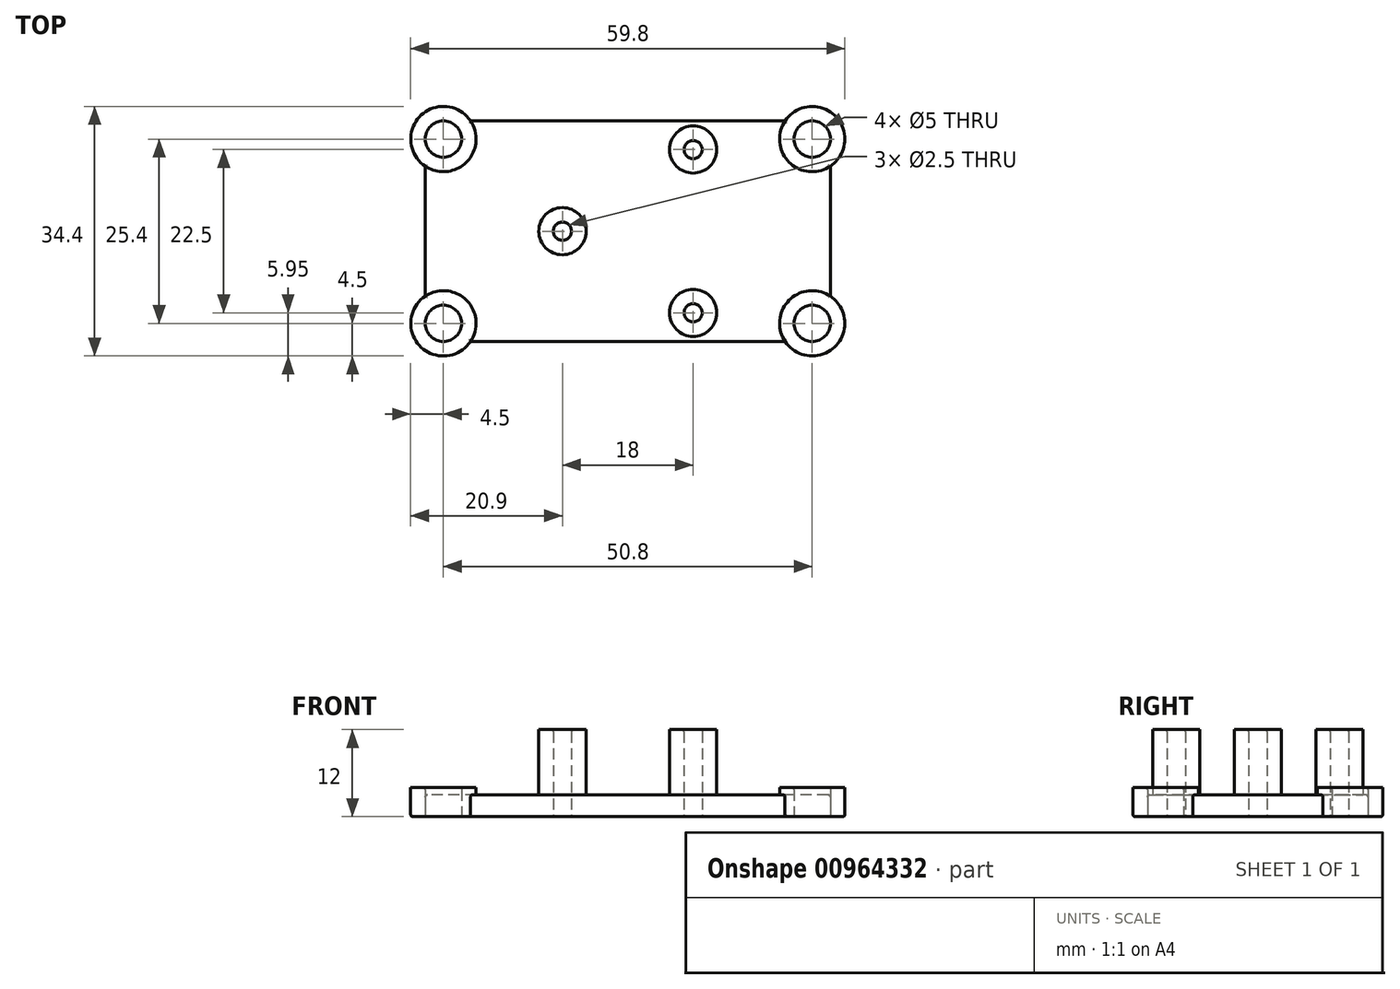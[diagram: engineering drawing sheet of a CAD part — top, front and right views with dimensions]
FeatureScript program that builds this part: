
annotation { "Feature Type Name" : "Feature", "Feature Type Description" : "" }
export const myFeature = defineFeature(function(context is Context, id is Id, definition is map)
    precondition{}
    {
        {
            var Q0;
            Q0=qCreatedBy(makeId("Top.planeOp"),FACE);
            var sketch = newSketch(context, id + "F0", { "sketchPlane" : qUnion([Q0])});
            skLineSegment(sketch, "E0.bottom", {"start": v(0, 0) * mm, "end": v(-18, 0) * mm, "construction": true});
            skLineSegment(sketch, "E0.top", {"start": v(0, 22.5) * mm, "end": v(-18, 22.5) * mm, "construction": true});
            skLineSegment(sketch, "E0.left", {"start": v(0, 0) * mm, "end": v(0, 22.5) * mm, "construction": true});
            skLineSegment(sketch, "E0.right", {"start": v(-18, 0) * mm, "end": v(-18, 22.5) * mm, "construction": true});
            skLineSegment(sketch, "E1", {"start": v(0, 11.25) * mm, "end": v(-18, 11.25) * mm, "construction": true});
            skLineSegment(sketch, "E2", {"start": v(-18, 11.25) * mm, "end": v(0, 22.5) * mm, "construction": true});
            skCircle(sketch, "E3", {"center": v(-18, 11.25) * mm, "radius": 1.25 * mm});
            skCircle(sketch, "E4", {"center": v(0, 22.5) * mm, "radius": 1.25 * mm});
            skCircle(sketch, "E5", {"center": v(0, 0) * mm, "radius": 1.25 * mm});
            skCircle(sketch, "E6", {"center": v(0, 22.5) * mm, "radius": 3.25 * mm});
            skCircle(sketch, "E7", {"center": v(-18, 11.25) * mm, "radius": 3.25 * mm});
            skCircle(sketch, "E8", {"center": v(0, 0) * mm, "radius": 3.25 * mm});
            skLineSegment(sketch, "E9.bottom", {"start": v(16.4, -1.45) * mm, "end": v(-34.4, -1.45) * mm, "construction": true});
            skLineSegment(sketch, "E9.top", {"start": v(16.4, 23.95) * mm, "end": v(-34.4, 23.95) * mm, "construction": true});
            skLineSegment(sketch, "E9.left", {"start": v(16.4, -1.45) * mm, "end": v(16.4, 23.95) * mm, "construction": true});
            skLineSegment(sketch, "E9.right", {"start": v(-34.4, -1.45) * mm, "end": v(-34.4, 23.95) * mm, "construction": true});
            skPoint(sketch, "E9.middle", {"position": v(-9, 11.25) * mm});
            skCircle(sketch, "E10", {"center": v(-34.4, 23.95) * mm, "radius": 2.5 * mm});
            skCircle(sketch, "E11", {"center": v(-34.4, -1.45) * mm, "radius": 2.5 * mm});
            skCircle(sketch, "E12", {"center": v(16.4, -1.45) * mm, "radius": 2.5 * mm});
            skCircle(sketch, "E13", {"center": v(16.4, 23.95) * mm, "radius": 2.5 * mm});
            skCircle(sketch, "E14", {"center": v(-34.4, 23.95) * mm, "radius": 4.5 * mm});
            skCircle(sketch, "E15", {"center": v(16.4, 23.95) * mm, "radius": 4.5 * mm});
            skCircle(sketch, "E16", {"center": v(-34.4, -1.45) * mm, "radius": 4.5 * mm});
            skCircle(sketch, "E17", {"center": v(16.4, -1.45) * mm, "radius": 4.5 * mm});
            skLineSegment(sketch, "E18.bottom", {"start": v(-34, 29.25) * mm, "end": v(16, 29.25) * mm, "construction": true});
            skLineSegment(sketch, "E18.top", {"start": v(-34, -6.75) * mm, "end": v(16, -6.75) * mm, "construction": true});
            skLineSegment(sketch, "E18.left", {"start": v(-34, 29.25) * mm, "end": v(-34, -6.75) * mm, "construction": true});
            skLineSegment(sketch, "E18.right", {"start": v(16, 29.25) * mm, "end": v(16, -6.75) * mm, "construction": true});
            skLineSegment(sketch, "E19", {"start": v(-34, 11.25) * mm, "end": v(16, 11.25) * mm, "construction": true});
            skLineSegment(sketch, "E20", {"start": v(-30.66, -3.95) * mm, "end": v(12.66, -3.95) * mm});
            skLineSegment(sketch, "E21", {"start": v(-36.9, 20.2) * mm, "end": v(-36.9, 2.3) * mm});
            skLineSegment(sketch, "E22", {"start": v(-30.66, 26.45) * mm, "end": v(12.66, 26.45) * mm});
            skLineSegment(sketch, "E23", {"start": v(18.9, 20.2) * mm, "end": v(18.9, 2.3) * mm});
            skSolve(sketch);
        }
        {
            var Q0;
            Q0=makeQuery(id+"F0.imprint","IMPRINT",FACE,{"disambiguationData":[TD([[makeQuery(id+"F0.imprint","IMPRINT",EDGE,{"derivedFrom":sQuery(id+"F0.wireOp",EDGE,"E6")}),-1.0]])]});
            extrude(context, id + "F1", {"entities" : qUnion([Q0]), "depth" : 3 * mm, "offsetDistance" : 25 * mm});
        }
        {
            var Q0;
            Q0=makeQuery(id+"F0.imprint","IMPRINT",FACE,{"disambiguationData":[TD([[makeQuery(id+"F0.imprint","IMPRINT",EDGE,{"derivedFrom":sQuery(id+"F0.wireOp",EDGE,"E4")}),-1.0]])]});
            var Q1;
            Q1=makeQuery(id+"F0.imprint","IMPRINT",FACE,{"disambiguationData":[TD([[makeQuery(id+"F0.imprint","IMPRINT",EDGE,{"derivedFrom":sQuery(id+"F0.wireOp",EDGE,"E3")}),-1.0]])]});
            var Q2;
            Q2=makeQuery(id+"F0.imprint","IMPRINT",FACE,{"disambiguationData":[TD([[makeQuery(id+"F0.imprint","IMPRINT",EDGE,{"derivedFrom":sQuery(id+"F0.wireOp",EDGE,"E5")}),-1.0]])]});
            extrude(context, id + "F2", {"entities" : qUnion([Q0, Q1, Q2]), "operationType" : NewBodyOperationType.ADD, "depth" : 12 * mm, "offsetDistance" : 25 * mm});
        }
        {
            var Q0;
            Q0=makeQuery(id+"F0.imprint","IMPRINT",FACE,{"disambiguationData":[TD([[makeQuery(id+"F0.imprint","IMPRINT",EDGE,{"derivedFrom":sQuery(id+"F0.wireOp",EDGE,"E10")}),-1.0]])]});
            var Q1;
            Q1=makeQuery(id+"F0.imprint","IMPRINT",FACE,{"disambiguationData":[TD([[makeQuery(id+"F0.imprint","IMPRINT",EDGE,{"derivedFrom":sQuery(id+"F0.wireOp",EDGE,"E13")}),-1.0]])]});
            var Q2;
            Q2=makeQuery(id+"F0.imprint","IMPRINT",FACE,{"disambiguationData":[TD([[makeQuery(id+"F0.imprint","IMPRINT",EDGE,{"derivedFrom":sQuery(id+"F0.wireOp",EDGE,"E11")}),-1.0]])]});
            var Q3;
            Q3=makeQuery(id+"F0.imprint","IMPRINT",FACE,{"disambiguationData":[TD([[makeQuery(id+"F0.imprint","IMPRINT",EDGE,{"derivedFrom":sQuery(id+"F0.wireOp",EDGE,"E12")}),-1.0]])]});
            extrude(context, id + "F3", {"entities" : qUnion([Q0, Q1, Q2, Q3]), "operationType" : NewBodyOperationType.ADD, "depth" : 4 * mm, "offsetDistance" : 25 * mm});
        }
        {
            var Q0;
            Q0=makeQuery(id+"F2.opExtrude","SWEPT_FACE",FACE,{"disambiguationData":[OSD([sQuery(id+"F0.wireOp",EDGE,"E3")])]});
            var Q1;
            Q1=makeQuery(id+"F3.opExtrude","SWEPT_FACE",FACE,{"disambiguationData":[OSD([sQuery(id+"F0.wireOp",EDGE,"E10")])]});
            var Q2;
            Q2=makeQuery(id+"F3.opExtrude","SWEPT_FACE",FACE,{"disambiguationData":[OSD([sQuery(id+"F0.wireOp",EDGE,"E11")])]});
            var Q3;
            Q3=makeQuery(id+"F2.opExtrude","SWEPT_FACE",FACE,{"disambiguationData":[OSD([sQuery(id+"F0.wireOp",EDGE,"E4")])]});
            var Q4;
            Q4=makeQuery(id+"F2.opExtrude","SWEPT_FACE",FACE,{"disambiguationData":[OSD([sQuery(id+"F0.wireOp",EDGE,"E5")])]});
            var Q5;
            Q5=makeQuery(id+"F3.opExtrude","SWEPT_FACE",FACE,{"disambiguationData":[OSD([sQuery(id+"F0.wireOp",EDGE,"E12")])]});
            var Q6;
            Q6=makeQuery(id+"F3.opExtrude","SWEPT_FACE",FACE,{"disambiguationData":[OSD([sQuery(id+"F0.wireOp",EDGE,"E13")])]});
            var Q7;
            {var subQ0=sQuery(id+"F0.wireOp",EDGE,"E15");var subQ1=sQuery(id+"F0.wireOp",EDGE,"E17");var subQ2=sQuery(id+"F0.wireOp",EDGE,"E16");var subQ3=sQuery(id+"F0.wireOp",EDGE,"E14");var subQ4=sQuery(id+"F0.wireOp",EDGE,"E8");var subQ5=sQuery(id+"F0.wireOp",EDGE,"E6");var subQ6=sQuery(id+"F0.wireOp",EDGE,"E7");Q7=makeQuery(id+"F3.boolean.opBoolean","MERGE",FACE,{"derivedFrom":[makeQuery(id+"F2.boolean.opBoolean","MERGE",FACE,{"derivedFrom":[makeQuery(id+"F1.opExtrude","CAP_FACE",FACE,{"disambiguationData":[OSD([subQ5,subQ6,subQ4,subQ3,subQ0,subQ2,subQ1,sQuery(id+"F0.wireOp",EDGE,"E20"),sQuery(id+"F0.wireOp",EDGE,"E21"),sQuery(id+"F0.wireOp",EDGE,"E22"),sQuery(id+"F0.wireOp",EDGE,"E23")])],"isStart":true}),makeQuery(id+"F2.opExtrude","CAP_FACE",FACE,{"disambiguationData":[OSD([sQuery(id+"F0.wireOp",EDGE,"E3"),subQ6])],"isStart":true}),makeQuery(id+"F2.opExtrude","CAP_FACE",FACE,{"disambiguationData":[OSD([sQuery(id+"F0.wireOp",EDGE,"E4"),subQ5])],"isStart":true}),makeQuery(id+"F2.opExtrude","CAP_FACE",FACE,{"disambiguationData":[OSD([sQuery(id+"F0.wireOp",EDGE,"E5"),subQ4])],"isStart":true})]}),makeQuery(id+"F3.opExtrude","CAP_FACE",FACE,{"disambiguationData":[OSD([sQuery(id+"F0.wireOp",EDGE,"E10"),subQ3])],"isStart":true}),makeQuery(id+"F3.opExtrude","CAP_FACE",FACE,{"disambiguationData":[OSD([sQuery(id+"F0.wireOp",EDGE,"E11"),subQ2])],"isStart":true}),makeQuery(id+"F3.opExtrude","CAP_FACE",FACE,{"disambiguationData":[OSD([sQuery(id+"F0.wireOp",EDGE,"E12"),subQ1])],"isStart":true}),makeQuery(id+"F3.opExtrude","CAP_FACE",FACE,{"disambiguationData":[OSD([sQuery(id+"F0.wireOp",EDGE,"E13"),subQ0])],"isStart":true})]});}
            var Q8;
            Q8=makeQuery(id+"F1.opExtrude","CAP_EDGE",EDGE,{"disambiguationData":[OSD([sQuery(id+"F0.wireOp",EDGE,"E7")])],"isStart":false});
            var Q9;
            Q9=makeQuery(id+"F1.opExtrude","CAP_EDGE",EDGE,{"disambiguationData":[OSD([sQuery(id+"F0.wireOp",EDGE,"E23")])],"isStart":false});
            var Q10;
            Q10=makeQuery(id+"F1.opExtrude","CAP_EDGE",EDGE,{"disambiguationData":[OSD([sQuery(id+"F0.wireOp",EDGE,"E22")])],"isStart":false});
            var Q11;
            Q11=makeQuery(id+"F1.opExtrude","CAP_EDGE",EDGE,{"disambiguationData":[OSD([sQuery(id+"F0.wireOp",EDGE,"E21")])],"isStart":false});
            var Q12;
            Q12=makeQuery(id+"F1.opExtrude","CAP_EDGE",EDGE,{"disambiguationData":[OSD([sQuery(id+"F0.wireOp",EDGE,"E20")])],"isStart":false});
            var Q13;
            Q13=makeQuery(id+"F1.opExtrude","CAP_EDGE",EDGE,{"disambiguationData":[OSD([sQuery(id+"F0.wireOp",EDGE,"E14")])],"isStart":false});
            var Q14;
            Q14=makeQuery(id+"F1.opExtrude","CAP_EDGE",EDGE,{"disambiguationData":[OSD([sQuery(id+"F0.wireOp",EDGE,"E16")])],"isStart":false});
            var Q15;
            Q15=makeQuery(id+"F1.opExtrude","CAP_EDGE",EDGE,{"disambiguationData":[OSD([sQuery(id+"F0.wireOp",EDGE,"E17")])],"isStart":false});
            var Q16;
            Q16=makeQuery(id+"F1.opExtrude","CAP_EDGE",EDGE,{"disambiguationData":[OSD([sQuery(id+"F0.wireOp",EDGE,"E15")])],"isStart":false});
            fillet(context, id + "F4", {"entities" : qUnion([Q0, Q1, Q2, Q3, Q4, Q5, Q6, Q7, Q8, Q9, Q10, Q11, Q12, Q13, Q14, Q15, Q16]), "tangentPropagation" : true, "radius" : 0.3 * mm, "defaultsChanged" : false, "vertexSettings" : [], "allowEdgeOverflow" : false});
        }
    });
